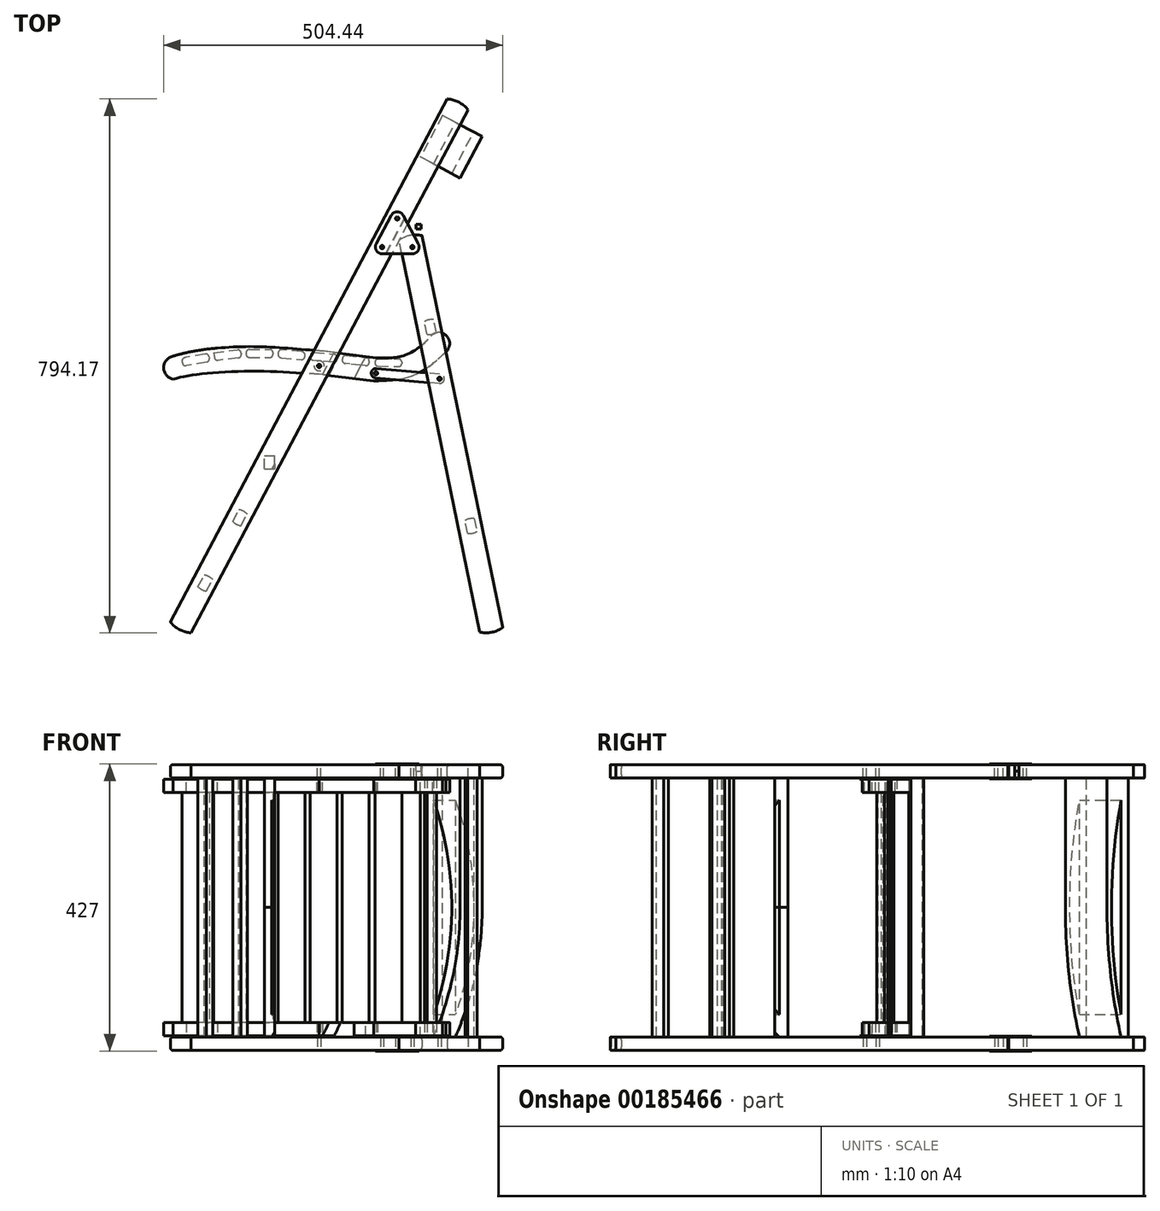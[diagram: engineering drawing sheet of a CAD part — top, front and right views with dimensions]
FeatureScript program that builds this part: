
annotation { "Feature Type Name" : "Feature", "Feature Type Description" : "" }
export const myFeature = defineFeature(function(context is Context, id is Id, definition is map)
    precondition{}
    {
        {
            var Q0;
            Q0=qCreatedBy(makeId("Top.planeOp"),FACE);
            var sketch = newSketch(context, id + "F0", { "sketchPlane" : qUnion([Q0])});
            skCircle(sketch, "E0", {"center": v(0, 0) * mm, "radius": 2.5 * mm});
            skLineSegment(sketch, "E1", {"start": v(-45, 8.94) * mm, "end": v(-45, -5.84) * mm, "construction": true});
            skCircle(sketch, "E2", {"center": v(-45, 0) * mm, "radius": 2.5 * mm});
            skLineSegment(sketch, "E3", {"start": v(-22.5, -17.7) * mm, "end": v(-22.5, 31.56) * mm, "construction": true});
            skLineSegment(sketch, "E4", {"start": v(-31.31, 42.5) * mm, "end": v(-6.98, 42.5) * mm, "construction": true});
            skLineSegment(sketch, "E5", {"start": v(-22.5, 31.56) * mm, "end": v(-22.5, 54.9) * mm, "construction": true});
            skCircle(sketch, "E6", {"center": v(-22.5, 42.5) * mm, "radius": 2.5 * mm});
            skLineSegment(sketch, "E7", {"start": v(-45, 0) * mm, "end": v(-62.32, 10) * mm, "construction": true});
            skLineSegment(sketch, "E8", {"start": v(-22.5, 42.5) * mm, "end": v(-47.11, 56.7) * mm, "construction": true});
            skLineSegment(sketch, "E9", {"start": v(-45, 0) * mm, "end": v(-22.5, 42.5) * mm, "construction": true});
            skPoint(sketch, "E10.start.orphan", {"position": v(-53.66, 5) * mm});
            skLineSegment(sketch, "E11", {"start": v(-33.5, 43.45) * mm, "end": v(-27.36, 54.08) * mm, "construction": true});
            skLineSegment(sketch, "E12", {"start": v(-53.66, 5) * mm, "end": v(-31.16, 47.5) * mm});
            skLineSegment(sketch, "E13.MirrorCS", {"start": v(8.66, 5) * mm, "end": v(-13.84, 47.5) * mm});
            skArc(sketch, "E14", {"start": v(-31.16, 47.5) * mm, "mid": v(-22.5, 52.5) * mm, "end": v(-13.84, 47.5) * mm});
            skLineSegment(sketch, "E15", {"start": v(-45, -10) * mm, "end": v(0, -10) * mm});
            skArc(sketch, "E16", {"start": v(-53.66, 5) * mm, "mid": v(-53.66, -5) * mm, "end": v(-45, -10) * mm});
            skArc(sketch, "E17", {"start": v(0, -10) * mm, "mid": v(8.66, -5) * mm, "end": v(8.66, 5) * mm});
            skLineSegment(sketch, "E18", {"start": v(51.83, 220.3) * mm, "end": v(-83.66, -35.63) * mm});
            skLineSegment(sketch, "E19.MirrorCS", {"start": v(82.76, 203.92) * mm, "end": v(-52.73, -52) * mm});
            skLineSegment(sketch, "E20", {"start": v(-22.5, 42.5) * mm, "end": v(-17.5, 51.16) * mm});
            skLineSegment(sketch, "E21", {"start": v(-22.5, 42.5) * mm, "end": v(72, 221) * mm, "construction": true});
            skArc(sketch, "E22", {"start": v(82.76, 203.92) * mm, "mid": v(69.1, 215.53) * mm, "end": v(51.83, 220.3) * mm});
            skLineSegment(sketch, "E23", {"start": v(51.83, 220.3) * mm, "end": v(-359.91, -557.44) * mm});
            skLineSegment(sketch, "E24", {"start": v(82.76, 203.92) * mm, "end": v(-328.98, -573.81) * mm});
            skLineSegment(sketch, "E25", {"start": v(-230.35, -128.17) * mm, "end": v(-2.2, -248.96) * mm, "construction": true});
            skArc(sketch, "E26.MirrorCS", {"start": v(51.83, 220.3) * mm, "mid": v(69.1, 215.53) * mm, "end": v(82.76, 203.92) * mm});
            skLineSegment(sketch, "E27.MirrorCS", {"start": v(-46.8, -225.34) * mm, "end": v(-274.96, -104.55) * mm, "construction": true});
            skArc(sketch, "E28.MirrorCS", {"start": v(-359.91, -557.44) * mm, "mid": v(-346.26, -569.05) * mm, "end": v(-328.98, -573.81) * mm});
            skArc(sketch, "E29.MirrorCS", {"start": v(-328.98, -573.81) * mm, "mid": v(-346.26, -569.05) * mm, "end": v(-359.91, -557.44) * mm});
            skLineSegment(sketch, "E30", {"start": v(-45, 0) * mm, "end": v(-155.4, -208.52) * mm, "construction": true});
            skCircle(sketch, "E31", {"center": v(-138.58, -176.76) * mm, "radius": 2.5 * mm});
            skArc(sketch, "E32", {"start": v(-112.68, -165.24) * mm, "mid": v(10.1, -199.75) * mm, "end": v(128.76, -153.04) * mm});
            skArc(sketch, "E33", {"start": v(-39.3, -26.62) * mm, "mid": v(29, -111.06) * mm, "end": v(36.3, -219.4) * mm});
            skLineSegment(sketch, "E34", {"start": v(0, 0) * mm, "end": v(40.4, -195.88) * mm, "construction": true});
            skLineSegment(sketch, "E35", {"start": v(40.4, -195.88) * mm, "end": v(43.8, -208.99) * mm, "construction": true});
            skCircle(sketch, "E36", {"center": v(40.4, -195.88) * mm, "radius": 2.5 * mm});
            skSolve(sketch);
        }
        {
            var Q0;
            Q0=makeQuery(id+"F0.imprint","IMPRINT",FACE,{"disambiguationData":[TD([[makeQuery(id+"F0.imprint","IMPRINT",EDGE,{"derivedFrom":sQuery(id+"F0.wireOp",EDGE,"E0")}),-1.0]])]});
            var Q1;
            Q1=makeQuery(id+"F0.imprint","IMPRINT",FACE,{"disambiguationData":[TD([[makeQuery(id+"F0.imprint","IMPRINT",EDGE,{"derivedFrom":sQuery(id+"F0.wireOp",EDGE,"E2")}),-1.0]])]});
            extrude(context, id + "F1", {"entities" : qUnion([Q0, Q1]), "depth" : 1 * mm});
        }
        {
            var Q0;
            {var subQ6=sQuery(id+"F0.wireOp",EDGE,"E12");Q0=makeQuery(id+"F0.imprint","IMPRINT",FACE,{"disambiguationData":[TD([[makeQuery(id+"F0.imprint","IMPRINT",EDGE,{"derivedFrom":subQ6}),1.0]])]});}
            var Q1;
            Q1=makeQuery(id+"F0.imprint","IMPRINT",FACE,{"disambiguationData":[TD([[makeQuery(id+"F0.imprint","IMPRINT",EDGE,{"derivedFrom":sQuery(id+"F0.wireOp",EDGE,"E2")}),-1.0]])]});
            extrude(context, id + "F2", {"entities" : qUnion([Q0, Q1]), "oppositeDirection" : true, "depth" : 20 * mm});
        }
        {
            var Q0;
            Q0=makeQuery(id+"F2.opExtrude","CAP_EDGE",EDGE,{"disambiguationData":[OSD([sQuery(id+"F0.wireOp",EDGE,"E23"),sQuery(id+"F0.wireOp",EDGE,"E18")])],"isStart":true});
            var Q1;
            Q1=makeQuery(id+"F2.opExtrude","CAP_EDGE",EDGE,{"disambiguationData":[OSD([sQuery(id+"F0.wireOp",EDGE,"E23"),sQuery(id+"F0.wireOp",EDGE,"E18")])],"isStart":false});
            fillet(context, id + "F3", {"entities" : qUnion([Q0, Q1]), "radius" : 5 * mm, "tangentPropagation" : true, "allowEdgeOverflow" : false});
        }
        {
            var Q0;
            Q0=qCreatedBy(makeId("Top.planeOp"),FACE);
            var sketch = newSketch(context, id + "F4", { "sketchPlane" : qUnion([Q0])});
            skPoint(sketch, "E37.0", {"position": v(-346.26, -569.05) * mm});
            skArc(sketch, "E38.0", {"start": v(-359.91, -557.44) * mm, "mid": v(-346.26, -569.05) * mm, "end": v(-328.98, -573.81) * mm});
            skLineSegment(sketch, "E39.0", {"start": v(82.76, 203.92) * mm, "end": v(-328.98, -573.81) * mm});
            skLineSegment(sketch, "E40", {"start": v(-409.38, -573.81) * mm, "end": v(185.16, -574.2) * mm, "construction": true});
            skLineSegment(sketch, "E41", {"start": v(185.16, -574.2) * mm, "end": v(553.68, -574.45) * mm, "construction": true});
            skLineSegment(sketch, "E42", {"start": v(0, 0) * mm, "end": v(132.92, -644.4) * mm, "construction": true});
            skLineSegment(sketch, "E43", {"start": v(100.28, -572.76) * mm, "end": v(-19.92, 9.96) * mm});
            skLineSegment(sketch, "E44", {"start": v(-326.85, -532.38) * mm, "end": v(180.53, -532.38) * mm, "construction": true});
            skArc(sketch, "E45", {"start": v(100.28, -572.76) * mm, "mid": v(118.2, -573.01) * mm, "end": v(134.55, -565.69) * mm});
            skArc(sketch, "E46", {"start": v(-19.92, 9.96) * mm, "mid": v(-3.57, 17.3) * mm, "end": v(14.35, 17.03) * mm});
            skLineSegment(sketch, "E47.trimOffspring", {"start": v(14.35, 17.03) * mm, "end": v(134.55, -565.69) * mm});
            skCircle(sketch, "E48", {"center": v(0, 0) * mm, "radius": 2.5 * mm});
            skSolve(sketch);
        }
        {
            var Q0;
            Q0 = qSketchRegion(id + "F4", true);
            extrude(context, id + "F5", {"entities" : qUnion([Q0]), "oppositeDirection" : true, "depth" : 20 * mm});
        }
        {
            var Q0;
            Q0=qCreatedBy(makeId("Top.planeOp"),FACE);
            var sketch = newSketch(context, id + "F6", { "sketchPlane" : qUnion([Q0])});
            skLineSegment(sketch, "E49.bottom", {"start": v(5.4, 33.88) * mm, "end": v(13.3, 33.88) * mm});
            skLineSegment(sketch, "E49.top", {"start": v(5.4, 27.1) * mm, "end": v(13.3, 27.1) * mm});
            skLineSegment(sketch, "E49.left", {"start": v(5.4, 33.88) * mm, "end": v(5.4, 27.1) * mm});
            skLineSegment(sketch, "E49.right", {"start": v(13.3, 33.88) * mm, "end": v(13.3, 27.1) * mm});
            skSolve(sketch);
        }
        {
            var Q0;
            Q0 = qSketchRegion(id + "F6", true);
            extrude(context, id + "F7", {"entities" : qUnion([Q0]), "oppositeDirection" : true, "depth" : 10 * mm});
        }
        {
            var Q0;
            Q0=makeQuery(id+"F7.opExtrude","CAP_FACE",FACE,{"disambiguationData":[OSD([sQuery(id+"F6.wireOp",EDGE,"E49.bottom"),sQuery(id+"F6.wireOp",EDGE,"E49.top"),sQuery(id+"F6.wireOp",EDGE,"E49.left"),sQuery(id+"F6.wireOp",EDGE,"E49.right")])],"isStart":false});
            var sketch = newSketch(context, id + "F8", { "sketchPlane" : qUnion([Q0])});
            skLineSegment(sketch, "E50.bottom", {"start": v(5.4, -33.88) * mm, "end": v(13.3, -33.88) * mm});
            skLineSegment(sketch, "E50.top", {"start": v(5.4, -27.1) * mm, "end": v(13.3, -27.1) * mm});
            skLineSegment(sketch, "E50.left", {"start": v(5.4, -33.88) * mm, "end": v(5.4, -27.1) * mm});
            skLineSegment(sketch, "E50.right", {"start": v(13.3, -33.88) * mm, "end": v(13.3, -27.1) * mm});
            skSolve(sketch);
        }
        {
            var Q0;
            Q0=makeQuery(id+"F1.opExtrude","SWEPT_BODY",BODY,{"disambiguationData":[OSD([sQuery(id+"F0.wireOp",EDGE,"E0"),sQuery(id+"F0.wireOp",EDGE,"E2"),sQuery(id+"F0.wireOp",EDGE,"E6"),sQuery(id+"F0.wireOp",EDGE,"E12"),sQuery(id+"F0.wireOp",EDGE,"E13.MirrorCS"),sQuery(id+"F0.wireOp",EDGE,"E14"),sQuery(id+"F0.wireOp",EDGE,"E15"),sQuery(id+"F0.wireOp",EDGE,"E16"),sQuery(id+"F0.wireOp",EDGE,"E17")])]});
            var Q1;
            Q1=makeQuery(id+"F7.opExtrude","SWEPT_BODY",BODY,{"disambiguationData":[OSD([sQuery(id+"F6.wireOp",EDGE,"E49.bottom"),sQuery(id+"F6.wireOp",EDGE,"E49.top"),sQuery(id+"F6.wireOp",EDGE,"E49.left"),sQuery(id+"F6.wireOp",EDGE,"E49.right")])]});
            var Q2;
            Q2=makeQuery(id+"F8.imprint","IMPRINT",FACE,{"disambiguationData":[TD([[makeQuery(id+"F8.imprint","IMPRINT",EDGE,{"derivedFrom":sQuery(id+"F8.wireOp",EDGE,"E50.bottom")}),1.0]])]});
            mirror(context, id + "F9", {"entities" : qUnion([Q0, Q1]), "mirrorPlane" : qUnion([Q2])});
        }
        {
            var Q0;
            Q0=makeQuery(id+"F0.imprint","IMPRINT",FACE,{"disambiguationData":[TD([[makeQuery(id+"F0.imprint","IMPRINT",EDGE,{"derivedFrom":sQuery(id+"F0.wireOp",EDGE,"E0")}),1.0]])]});
            var Q1;
            {var subQ0=sQuery(id+"F0.wireOp",EDGE,"E36");var subQ1=sQuery(id+"F0.wireOp",EDGE,"E32");var subQ2=makeQuery(id+"F0.imprint","INTERSECT",VERTEX,{"disambiguationData":[OD(0.0)],"derivedFrom":[subQ1,subQ0]});Q1=makeQuery(id+"F0.imprint","IMPRINT",FACE,{"disambiguationData":[TD([[makeQuery(id+"F0.imprint","IMPRINT",EDGE,{"disambiguationData":[TD([[subQ2,1.0]])],"derivedFrom":subQ1}),-1.0]])]});}
            var Q2;
            {var subQ0=sQuery(id+"F0.wireOp",EDGE,"E36");var subQ1=sQuery(id+"F0.wireOp",EDGE,"E32");var subQ2=makeQuery(id+"F0.imprint","INTERSECT",VERTEX,{"disambiguationData":[OD(1.0)],"derivedFrom":[subQ1,subQ0]});Q2=makeQuery(id+"F0.imprint","IMPRINT",FACE,{"disambiguationData":[TD([[makeQuery(id+"F0.imprint","IMPRINT",EDGE,{"disambiguationData":[TD([[subQ2,-1.0]])],"derivedFrom":subQ1}),1.0]])]});}
            var Q3;
            {var subQ0=sQuery(id+"F0.wireOp",EDGE,"E36");var subQ1=sQuery(id+"F0.wireOp",EDGE,"E32");var subQ2=makeQuery(id+"F0.imprint","INTERSECT",VERTEX,{"disambiguationData":[OD(0.0)],"derivedFrom":[subQ1,subQ0]});Q3=makeQuery(id+"F0.imprint","IMPRINT",FACE,{"disambiguationData":[TD([[makeQuery(id+"F0.imprint","IMPRINT",EDGE,{"disambiguationData":[TD([[subQ2,1.0]])],"derivedFrom":subQ1}),1.0]])]});}
            var Q4;
            {var subQ0=sQuery(id+"F0.wireOp",EDGE,"E36");var subQ1=sQuery(id+"F0.wireOp",EDGE,"E32");var subQ2=makeQuery(id+"F0.imprint","INTERSECT",VERTEX,{"disambiguationData":[OD(1.0)],"derivedFrom":[subQ1,subQ0]});Q4=makeQuery(id+"F0.imprint","IMPRINT",FACE,{"disambiguationData":[TD([[makeQuery(id+"F0.imprint","IMPRINT",EDGE,{"disambiguationData":[TD([[subQ2,-1.0]])],"derivedFrom":subQ1}),-1.0]])]});}
            extrude(context, id + "F10", {"entities" : qUnion([Q0, Q1, Q2, Q3, Q4]), "operationType" : NewBodyOperationType.REMOVE, "oppositeDirection" : true, "depth" : 200 * mm});
        }
        {
            var Q0;
            Q0=makeQuery(id+"F5.opExtrude","CAP_EDGE",EDGE,{"disambiguationData":[OSD([sQuery(id+"F4.wireOp",EDGE,"E47.trimOffspring")])],"isStart":true});
            var Q1;
            Q1=makeQuery(id+"F5.opExtrude","CAP_EDGE",EDGE,{"disambiguationData":[OSD([sQuery(id+"F4.wireOp",EDGE,"E47.trimOffspring")])],"isStart":false});
            fillet(context, id + "F11", {"entities" : qUnion([Q0, Q1]), "radius" : 5 * mm, "tangentPropagation" : true, "allowEdgeOverflow" : false});
        }
        {
            var Q0;
            Q0=makeQuery(id+"F2.opExtrude","CAP_FACE",FACE,{"disambiguationData":[OSD([sQuery(id+"F0.wireOp",EDGE,"E2"),sQuery(id+"F0.wireOp",EDGE,"E6"),sQuery(id+"F0.wireOp",EDGE,"E23"),sQuery(id+"F0.wireOp",EDGE,"E24"),sQuery(id+"F0.wireOp",EDGE,"E18"),sQuery(id+"F0.wireOp",EDGE,"E26.MirrorCS"),sQuery(id+"F0.wireOp",EDGE,"E29.MirrorCS"),sQuery(id+"F0.wireOp",EDGE,"E31")])],"isStart":false});
            var sketch = newSketch(context, id + "F12", { "sketchPlane" : qUnion([Q0])});
            skLineSegment(sketch, "E51.0", {"start": v(51.83, -220.3) * mm, "end": v(-359.91, 557.44) * mm});
            skLineSegment(sketch, "E52.0", {"start": v(82.76, -203.92) * mm, "end": v(-328.98, 573.81) * mm});
            skLineSegment(sketch, "E53.0", {"start": v(100.28, 572.76) * mm, "end": v(-19.92, -9.96) * mm});
            skLineSegment(sketch, "E54", {"start": v(-319.26, 506.3) * mm, "end": v(-309.5, 487.86) * mm});
            skLineSegment(sketch, "E55", {"start": v(82.26, 426.01) * mm, "end": v(78.28, 406.7) * mm});
            skLineSegment(sketch, "E56", {"start": v(84.9, 404.17) * mm, "end": v(84.9, 404.17) * mm});
            skLineSegment(sketch, "E57", {"start": v(91.99, 403.88) * mm, "end": v(95.97, 423.18) * mm});
            skPoint(sketch, "E58.0", {"position": v(115.55, 573.47) * mm});
            skLineSegment(sketch, "E59", {"start": v(21.9, 130.1) * mm, "end": v(17.92, 110.8) * mm});
            skLineSegment(sketch, "E60", {"start": v(35.62, 127.27) * mm, "end": v(31.64, 107.97) * mm});
            skArc(sketch, "E61", {"start": v(89.35, 425.72) * mm, "mid": v(85.81, 426.15) * mm, "end": v(82.26, 426.01) * mm});
            skArc(sketch, "E62", {"start": v(89.35, 425.72) * mm, "mid": v(92.76, 424.72) * mm, "end": v(95.97, 423.18) * mm});
            skPoint(sketch, "E63.MirrorCS.start.orphan", {"position": v(89.35, 425.72) * mm});
            skArc(sketch, "E64", {"start": v(91.99, 403.88) * mm, "mid": v(84.9, 404.17) * mm, "end": v(78.28, 406.7) * mm});
            skArc(sketch, "E65", {"start": v(29, 129.8) * mm, "mid": v(25.46, 130.24) * mm, "end": v(21.9, 130.1) * mm});
            skArc(sketch, "E66", {"start": v(21.9, 130.1) * mm, "mid": v(29, 129.8) * mm, "end": v(35.62, 127.27) * mm});
            skArc(sketch, "E67", {"start": v(24.55, 108.26) * mm, "mid": v(28.08, 107.83) * mm, "end": v(31.64, 107.97) * mm});
            skArc(sketch, "E68", {"start": v(31.64, 107.97) * mm, "mid": v(24.55, 108.26) * mm, "end": v(17.92, 110.8) * mm});
            skLineSegment(sketch, "E69", {"start": v(-306.9, 512.85) * mm, "end": v(-297.13, 494.42) * mm});
            skPoint(sketch, "E70.0", {"position": v(-343.85, 570.22) * mm});
            skArc(sketch, "E71", {"start": v(-313.08, 509.57) * mm, "mid": v(-316.08, 507.66) * mm, "end": v(-318.73, 505.29) * mm});
            skArc(sketch, "E72", {"start": v(-318.73, 505.29) * mm, "mid": v(-313.08, 509.57) * mm, "end": v(-306.36, 511.84) * mm});
            skArc(sketch, "E73", {"start": v(-302.78, 490.13) * mm, "mid": v(-299.78, 492.04) * mm, "end": v(-297.13, 494.42) * mm});
            skArc(sketch, "E74", {"start": v(-297.13, 494.42) * mm, "mid": v(-302.78, 490.13) * mm, "end": v(-309.5, 487.86) * mm});
            skArc(sketch, "E75", {"start": v(-251.32, 392.91) * mm, "mid": v(-254.58, 391.5) * mm, "end": v(-258.04, 390.65) * mm});
            skArc(sketch, "E76", {"start": v(-258.04, 390.65) * mm, "mid": v(-251.32, 392.91) * mm, "end": v(-245.66, 397.2) * mm});
            skArc(sketch, "E77", {"start": v(-261.6, 412.36) * mm, "mid": v(-258.34, 413.76) * mm, "end": v(-254.89, 414.62) * mm});
            skArc(sketch, "E78", {"start": v(-254.89, 414.62) * mm, "mid": v(-261.6, 412.36) * mm, "end": v(-267.26, 408.07) * mm});
            skLineSegment(sketch, "E79.trimOffspring", {"start": v(-254.89, 414.62) * mm, "end": v(-245.66, 397.2) * mm});
            skLineSegment(sketch, "E80.trimOffspring", {"start": v(-267.26, 408.07) * mm, "end": v(-258.04, 390.65) * mm});
            skSolve(sketch);
        }
        {
            var Q0;
            Q0 = qSketchRegion(id + "F12", true);
            extrude(context, id + "F13", {"entities" : qUnion([Q0]), "depth" : 385 * mm});
        }
        {
            var Q0;
            Q0=makeQuery(id+"F2.opExtrude","CAP_FACE",FACE,{"disambiguationData":[OSD([sQuery(id+"F0.wireOp",EDGE,"E2"),sQuery(id+"F0.wireOp",EDGE,"E6"),sQuery(id+"F0.wireOp",EDGE,"E23"),sQuery(id+"F0.wireOp",EDGE,"E24"),sQuery(id+"F0.wireOp",EDGE,"E18"),sQuery(id+"F0.wireOp",EDGE,"E26.MirrorCS"),sQuery(id+"F0.wireOp",EDGE,"E29.MirrorCS"),sQuery(id+"F0.wireOp",EDGE,"E31")])],"isStart":false});
            var sketch = newSketch(context, id + "F14", { "sketchPlane" : qUnion([Q0])});
            skLineSegment(sketch, "E81.bottom", {"start": v(-219.73, 329.93) * mm, "end": v(-205.06, 329.93) * mm});
            skLineSegment(sketch, "E81.top", {"start": v(-219.73, 309.99) * mm, "end": v(-205.06, 309.99) * mm});
            skLineSegment(sketch, "E81.left", {"start": v(-219.73, 329.93) * mm, "end": v(-219.73, 309.99) * mm});
            skLineSegment(sketch, "E81.right", {"start": v(-205.06, 329.93) * mm, "end": v(-205.06, 309.99) * mm});
            skSolve(sketch);
        }
        {
            var Q0;
            Q0 = qSketchRegion(id + "F14", true);
            extrude(context, id + "F15", {"entities" : qUnion([Q0]), "depth" : 192.5 * mm});
        }
        {
            var Q0;
            Q0=makeQuery(id+"F15.opExtrude","CAP_FACE",FACE,{"disambiguationData":[OSD([sQuery(id+"F14.wireOp",EDGE,"E81.bottom"),sQuery(id+"F14.wireOp",EDGE,"E81.top"),sQuery(id+"F14.wireOp",EDGE,"E81.left"),sQuery(id+"F14.wireOp",EDGE,"E81.right")])],"isStart":false});
            var sketch = newSketch(context, id + "F16", { "sketchPlane" : qUnion([Q0])});
            skSolve(sketch);
        }
        {
            var Q0;
            Q0=makeQuery(id+"F2.opExtrude","SWEPT_BODY",BODY,{"disambiguationData":[OSD([sQuery(id+"F0.wireOp",EDGE,"E2"),sQuery(id+"F0.wireOp",EDGE,"E6"),sQuery(id+"F0.wireOp",EDGE,"E23"),sQuery(id+"F0.wireOp",EDGE,"E24"),sQuery(id+"F0.wireOp",EDGE,"E18"),sQuery(id+"F0.wireOp",EDGE,"E26.MirrorCS"),sQuery(id+"F0.wireOp",EDGE,"E29.MirrorCS"),sQuery(id+"F0.wireOp",EDGE,"E31")])]});
            var Q1;
            Q1=makeQuery(id+"F5.opExtrude","SWEPT_BODY",BODY,{"disambiguationData":[OSD([sQuery(id+"F4.wireOp",EDGE,"E43"),sQuery(id+"F4.wireOp",EDGE,"E45"),sQuery(id+"F4.wireOp",EDGE,"E46"),sQuery(id+"F4.wireOp",EDGE,"E47.trimOffspring"),sQuery(id+"F4.wireOp",EDGE,"E48")])]});
            var Q2;
            Q2=makeQuery(id+"F9.opPattern","COPY",BODY,{"derivedFrom":makeQuery(id+"F1.opExtrude","SWEPT_BODY",BODY,{"disambiguationData":[OSD([sQuery(id+"F0.wireOp",EDGE,"E0"),sQuery(id+"F0.wireOp",EDGE,"E2"),sQuery(id+"F0.wireOp",EDGE,"E6"),sQuery(id+"F0.wireOp",EDGE,"E12"),sQuery(id+"F0.wireOp",EDGE,"E13.MirrorCS"),sQuery(id+"F0.wireOp",EDGE,"E14"),sQuery(id+"F0.wireOp",EDGE,"E15"),sQuery(id+"F0.wireOp",EDGE,"E16"),sQuery(id+"F0.wireOp",EDGE,"E17")])]}),"instanceName":"1"});
            var Q3;
            Q3=makeQuery(id+"F1.opExtrude","SWEPT_BODY",BODY,{"disambiguationData":[OSD([sQuery(id+"F0.wireOp",EDGE,"E0"),sQuery(id+"F0.wireOp",EDGE,"E2"),sQuery(id+"F0.wireOp",EDGE,"E6"),sQuery(id+"F0.wireOp",EDGE,"E12"),sQuery(id+"F0.wireOp",EDGE,"E13.MirrorCS"),sQuery(id+"F0.wireOp",EDGE,"E14"),sQuery(id+"F0.wireOp",EDGE,"E15"),sQuery(id+"F0.wireOp",EDGE,"E16"),sQuery(id+"F0.wireOp",EDGE,"E17")])]});
            var Q4;
            Q4=makeQuery(id+"F13.opExtrude","SWEPT_BODY",BODY,{"disambiguationData":[OSD([sQuery(id+"F12.wireOp",EDGE,"E55"),sQuery(id+"F12.wireOp",EDGE,"E57"),sQuery(id+"F12.wireOp",EDGE,"E61"),sQuery(id+"F12.wireOp",EDGE,"E62"),sQuery(id+"F12.wireOp",EDGE,"E64")])]});
            var Q5;
            Q5=makeQuery(id+"F13.opExtrude","SWEPT_BODY",BODY,{"disambiguationData":[OSD([sQuery(id+"F12.wireOp",EDGE,"E59"),sQuery(id+"F12.wireOp",EDGE,"E60"),sQuery(id+"F12.wireOp",EDGE,"E66"),sQuery(id+"F12.wireOp",EDGE,"E68")])]});
            var Q6;
            Q6=makeQuery(id+"F13.opExtrude","SWEPT_BODY",BODY,{"disambiguationData":[OSD([sQuery(id+"F12.wireOp",EDGE,"E54"),sQuery(id+"F12.wireOp",EDGE,"E69"),sQuery(id+"F12.wireOp",EDGE,"E72"),sQuery(id+"F12.wireOp",EDGE,"E74")])]});
            var Q7;
            Q7=makeQuery(id+"F15.opExtrude","SWEPT_BODY",BODY,{"disambiguationData":[OSD([sQuery(id+"F14.wireOp",EDGE,"E81.bottom"),sQuery(id+"F14.wireOp",EDGE,"E81.top"),sQuery(id+"F14.wireOp",EDGE,"E81.left"),sQuery(id+"F14.wireOp",EDGE,"E81.right")])]});
            var Q8;
            Q8=makeQuery(id+"F13.opExtrude","SWEPT_BODY",BODY,{"disambiguationData":[OSD([sQuery(id+"F12.wireOp",EDGE,"E76"),sQuery(id+"F12.wireOp",EDGE,"E78"),sQuery(id+"F12.wireOp",EDGE,"E79.trimOffspring"),sQuery(id+"F12.wireOp",EDGE,"E80.trimOffspring")])]});
            var Q9;
            Q9=makeQuery(id+"F16.imprint","IMPRINT",FACE,{"disambiguationData":[TD([[makeQuery(id+"F16.imprint","IMPRINT",EDGE,{"derivedFrom":makeQuery(id+"F15.opExtrude","CAP_EDGE",EDGE,{"disambiguationData":[OSD([sQuery(id+"F14.wireOp",EDGE,"E81.bottom")])],"isStart":false})}),-1.0]])]});
            mirror(context, id + "F17", {"entities" : qUnion([Q0, Q1, Q2, Q3, Q4, Q5, Q6, Q7, Q8]), "mirrorPlane" : qUnion([Q9])});
        }
        {
            var Q0;
            Q0=makeQuery(id+"F5.opExtrude","CAP_FACE",FACE,{"disambiguationData":[OSD([sQuery(id+"F4.wireOp",EDGE,"E43"),sQuery(id+"F4.wireOp",EDGE,"E45"),sQuery(id+"F4.wireOp",EDGE,"E46"),sQuery(id+"F4.wireOp",EDGE,"E47.trimOffspring"),sQuery(id+"F4.wireOp",EDGE,"E48")])],"isStart":false});
            var sketch = newSketch(context, id + "F18", { "sketchPlane" : qUnion([Q0])});
            skCircle(sketch, "E82.0", {"center": v(40.4, 195.88) * mm, "radius": 2.5 * mm});
            skArc(sketch, "E83", {"start": v(-49.74, 165.88) * mm, "mid": v(-52.25, 216.86) * mm, "end": v(-28.02, 261.78) * mm, "construction": true});
            skLineSegment(sketch, "E84", {"start": v(118.73, 195.88) * mm, "end": v(-61.62, 195.88) * mm, "construction": true});
            skLineSegment(sketch, "E85", {"start": v(40.4, 195.88) * mm, "end": v(-61.21, 186.99) * mm, "construction": true});
            skCircle(sketch, "E86", {"center": v(-54.23, 187.6) * mm, "radius": 2.5 * mm});
            skLineSegment(sketch, "E87", {"start": v(41.62, 188.96) * mm, "end": v(-53.88, 180.6) * mm});
            skLineSegment(sketch, "E88.MirrorCS", {"start": v(40.4, 202.9) * mm, "end": v(-55.1, 194.55) * mm});
            skArc(sketch, "E89", {"start": v(-53.37, 180.65) * mm, "mid": v(-61.21, 186.99) * mm, "end": v(-54.59, 194.6) * mm});
            skArc(sketch, "E90", {"start": v(40.4, 188.85) * mm, "mid": v(47.43, 195.88) * mm, "end": v(40.4, 202.9) * mm});
            skSolve(sketch);
        }
        {
            var Q0;
            Q0 = qSketchRegion(id + "F18", true);
            extrude(context, id + "F19", {"entities" : qUnion([Q0]), "depth" : 1.5 * mm});
        }
        {
            var Q0;
            Q0=makeQuery(id+"F19.opExtrude","SWEPT_BODY",BODY,{"disambiguationData":[OSD([sQuery(id+"F18.wireOp",EDGE,"E86"),sQuery(id+"F18.wireOp",EDGE,"E87"),sQuery(id+"F18.wireOp",EDGE,"E88.MirrorCS"),sQuery(id+"F18.wireOp",EDGE,"E89"),sQuery(id+"F18.wireOp",EDGE,"E90"),sQuery(id+"F18.wireOp",EDGE,"E82.0")])]});
            var Q1;
            Q1=makeQuery(id+"F17.opPattern","COPY",FACE,{"derivedFrom":makeQuery(id+"F15.opExtrude","CAP_FACE",FACE,{"disambiguationData":[OSD([sQuery(id+"F14.wireOp",EDGE,"E81.bottom"),sQuery(id+"F14.wireOp",EDGE,"E81.top"),sQuery(id+"F14.wireOp",EDGE,"E81.left"),sQuery(id+"F14.wireOp",EDGE,"E81.right")])],"isStart":false}),"instanceName":"1"});
            mirror(context, id + "F20", {"entities" : qUnion([Q0]), "mirrorPlane" : qUnion([Q1])});
        }
        {
            var Q0;
            Q0=makeQuery(id+"F2.opExtrude","CAP_FACE",FACE,{"disambiguationData":[OSD([sQuery(id+"F0.wireOp",EDGE,"E2"),sQuery(id+"F0.wireOp",EDGE,"E6"),sQuery(id+"F0.wireOp",EDGE,"E23"),sQuery(id+"F0.wireOp",EDGE,"E24"),sQuery(id+"F0.wireOp",EDGE,"E18"),sQuery(id+"F0.wireOp",EDGE,"E26.MirrorCS"),sQuery(id+"F0.wireOp",EDGE,"E29.MirrorCS"),sQuery(id+"F0.wireOp",EDGE,"E31")])],"isStart":false});
            var sketch = newSketch(context, id + "F21", { "sketchPlane" : qUnion([Q0])});
            skCircle(sketch, "E91", {"center": v(-138.58, 176.76) * mm, "radius": 2.5 * mm});
            skCircle(sketch, "E92", {"center": v(-138.58, 176.76) * mm, "radius": 7.5 * mm});
            skSolve(sketch);
        }
        {
            var Q0;
            Q0 = qSketchRegion(id + "F21", true);
            extrude(context, id + "F22", {"entities" : qUnion([Q0]), "depth" : 1.5 * mm});
        }
        {
            var Q0;
            Q0=makeQuery(id+"F19.opExtrude","CAP_FACE",FACE,{"disambiguationData":[OSD([sQuery(id+"F18.wireOp",EDGE,"E86"),sQuery(id+"F18.wireOp",EDGE,"E87"),sQuery(id+"F18.wireOp",EDGE,"E88.MirrorCS"),sQuery(id+"F18.wireOp",EDGE,"E89"),sQuery(id+"F18.wireOp",EDGE,"E90"),sQuery(id+"F18.wireOp",EDGE,"E82.0")])],"isStart":false});
            var sketch = newSketch(context, id + "F23", { "sketchPlane" : qUnion([Q0])});
            skArc(sketch, "E93", {"start": v(64.27, 168.7) * mm, "mid": v(29.96, 102.09) * mm, "end": v(-37.18, 68.81) * mm, "construction": true});
            skLineSegment(sketch, "E94", {"start": v(-57.48, 199.15) * mm, "end": v(-57.54, 199.14) * mm});
            skPoint(sketch, "E94.endSnap0", {"position": v(-138.54, 189.15) * mm});
            skPoint(sketch, "E95.endSnap0", {"position": v(-133.82, 154.74) * mm});
            skPoint(sketch, "E96.trimOffspring.end.orphan", {"position": v(-145.21, 154.74) * mm});
            skLineSegment(sketch, "E97", {"start": v(-53.82, 164.6) * mm, "end": v(-133.82, 154.74) * mm});
            skLineSegment(sketch, "E98", {"start": v(-57.48, 199.15) * mm, "end": v(-138.54, 189.15) * mm});
            skArc(sketch, "E99", {"start": v(47.11, 172.28) * mm, "mid": v(25.17, 122.78) * mm, "end": v(-18.93, 91.37) * mm, "construction": true});
            skFitSpline(sketch, "E100", {"points": [v(-53.82, 164.6) * mm, v(0, 155.78) * mm, v(30.24, 129.54) * mm, v(30.22, 129.52) * mm], "startDerivative": vector(101.7, 4.07) * mm, "endDerivative": vector(-2.24, -0.94) * mm});
            skArc(sketch, "E101", {"start": v(30.24, 129.54) * mm, "mid": v(52.29, 133.76) * mm, "end": v(49.6, 156.05) * mm});
            skFitSpline(sketch, "E102", {"points": [v(-57.54, 199.14) * mm, v(4.84, 189.2) * mm, v(49.6, 156.05) * mm], "startDerivative": vector(128.56, -6.46) * mm, "endDerivative": vector(85.52, -80.44) * mm});
            skFitSpline(sketch, "E103", {"points": [v(-133.82, 154.74) * mm, v(-243.2, 148.03) * mm, v(-324.06, 154.74) * mm, v(-356.53, 162.44) * mm], "startDerivative": vector(-266.22, -22.84) * mm, "endDerivative": vector(-122.92, 37.02) * mm});
            skLineSegment(sketch, "E104", {"start": v(-138.54, 189.15) * mm, "end": v(-138.54, 189.15) * mm});
            skFitSpline(sketch, "E105", {"points": [v(-138.54, 189.15) * mm, v(-231.03, 184.64) * mm, v(-317.3, 189.15) * mm, v(-356.14, 196.54) * mm], "startDerivative": vector(-237.1, -15.36) * mm, "endDerivative": vector(-134.36, 39.6) * mm});
            skArc(sketch, "E106", {"start": v(-356.14, 196.54) * mm, "mid": v(-369.9, 179.56) * mm, "end": v(-356.36, 162.4) * mm});
            skFitSpline(sketch, "E107", {"points": [v(-133.82, 154.74) * mm, v(-221.72, 148.83) * mm, v(-296.47, 150.88) * mm, v(-338.72, 157.7) * mm, v(-356.36, 162.4) * mm, v(-356.42, 162.42) * mm], "startDerivative": vector(-276.14, -22.14) * mm, "endDerivative": vector(-3.9, 0.81) * mm});
            skCircle(sketch, "E108", {"center": v(-54.23, 187.6) * mm, "radius": 2.5 * mm});
            skCircle(sketch, "E109", {"center": v(-139.52, 177.02) * mm, "radius": 2.5 * mm});
            skPoint(sketch, "E110.orphan", {"position": v(-66.23, 187.6) * mm});
            skLineSegment(sketch, "E111.trimOffspring", {"start": v(-57.54, 199.14) * mm, "end": v(-57.54, 199.14) * mm});
            skPoint(sketch, "E112.orphan", {"position": v(-151.52, 177.02) * mm});
            skFitSpline(sketch, "E113", {"points": [v(-57.48, 199.15) * mm, v(-35.44, 198.03) * mm, v(4.84, 189.2) * mm, v(44.67, 160.68) * mm, v(49.6, 156.05) * mm], "startDerivative": vector(90.74, -3.96) * mm, "endDerivative": vector(28.38, -27.6) * mm});
            skSolve(sketch);
        }
        {
            var Q0;
            Q0 = qSketchRegion(id + "F23", true);
            extrude(context, id + "F24", {"entities" : qUnion([Q0]), "depth" : 20 * mm});
        }
        {
            var Q0;
            Q0=makeQuery(id+"F24.opExtrude","SWEPT_BODY",BODY,{"disambiguationData":[OSD([sQuery(id+"F23.wireOp",EDGE,"E97"),sQuery(id+"F23.wireOp",EDGE,"E98"),sQuery(id+"F23.wireOp",EDGE,"E100"),sQuery(id+"F23.wireOp",EDGE,"E101"),sQuery(id+"F23.wireOp",EDGE,"E105"),sQuery(id+"F23.wireOp",EDGE,"E106"),sQuery(id+"F23.wireOp",EDGE,"E107"),sQuery(id+"F23.wireOp",EDGE,"E108"),sQuery(id+"F23.wireOp",EDGE,"E109"),sQuery(id+"F23.wireOp",EDGE,"E113")])]});
            var Q1;
            Q1=makeQuery(id+"F17.opPattern","COPY",FACE,{"derivedFrom":makeQuery(id+"F15.opExtrude","CAP_FACE",FACE,{"disambiguationData":[OSD([sQuery(id+"F14.wireOp",EDGE,"E81.bottom"),sQuery(id+"F14.wireOp",EDGE,"E81.top"),sQuery(id+"F14.wireOp",EDGE,"E81.left"),sQuery(id+"F14.wireOp",EDGE,"E81.right")])],"isStart":false}),"instanceName":"1"});
            mirror(context, id + "F25", {"entities" : qUnion([Q0]), "mirrorPlane" : qUnion([Q1])});
        }
        {
            var Q0;
            Q0=makeQuery(id+"F17.opPattern","COPY",FACE,{"derivedFrom":makeQuery(id+"F2.opExtrude","SWEPT_FACE",FACE,{"disambiguationData":[OSD([sQuery(id+"F0.wireOp",EDGE,"E24")])]}),"instanceName":"1"});
            var sketch = newSketch(context, id + "F26", { "sketchPlane" : qUnion([Q0])});
            skLineSegment(sketch, "E114.0", {"start": v(218.95, -405) * mm, "end": v(-661.05, -405) * mm});
            skLineSegment(sketch, "E115.0", {"start": v(218.95, -20) * mm, "end": v(-661.05, -20) * mm});
            skPoint(sketch, "E116.0", {"position": v(218.95, -415) * mm});
            skPoint(sketch, "E117.0", {"position": v(218.95, 0) * mm});
            skLineSegment(sketch, "E118.0", {"start": v(218.95, -20) * mm, "end": v(218.95, 0) * mm});
            skLineSegment(sketch, "E119.bottom", {"start": v(193.95, -405) * mm, "end": v(123.95, -405) * mm});
            skLineSegment(sketch, "E119.top", {"start": v(193.95, -20) * mm, "end": v(123.95, -20) * mm});
            skLineSegment(sketch, "E119.left", {"start": v(193.95, -405) * mm, "end": v(193.95, -20) * mm});
            skLineSegment(sketch, "E119.right", {"start": v(123.95, -405) * mm, "end": v(123.95, -20) * mm});
            skSolve(sketch);
        }
        {
            var Q0;
            Q0 = qSketchRegion(id + "F26", true);
            extrude(context, id + "F27", {"entities" : qUnion([Q0]), "depth" : 37 * mm});
        }
        {
            var Q0;
            Q0=makeQuery(id+"F27.opExtrude","CAP_FACE",FACE,{"disambiguationData":[OSD([sQuery(id+"F26.wireOp",EDGE,"E119.bottom"),sQuery(id+"F26.wireOp",EDGE,"E119.top"),sQuery(id+"F26.wireOp",EDGE,"E119.left"),sQuery(id+"F26.wireOp",EDGE,"E119.right")])],"isStart":true});
            extrude(context, id + "F28", {"entities" : qUnion([Q0]), "operationType" : NewBodyOperationType.ADD, "depth" : 30 * mm});
        }
        {
            var Q0;
            {var subQ0=sQuery(id+"F26.wireOp",EDGE,"E119.left");Q0=makeQuery(id+"F28.boolean.opBoolean","MERGE",FACE,{"derivedFrom":[makeQuery(id+"F27.opExtrude","SWEPT_FACE",FACE,{"disambiguationData":[OSD([subQ0])]}),makeQuery(id+"F28.opExtrude","SWEPT_FACE",FACE,{"disambiguationData":[OSD([subQ0])]})]});}
            var sketch = newSketch(context, id + "F29", { "sketchPlane" : qUnion([Q0])});
            skLineSegment(sketch, "E120.0", {"start": v(-14.73, -405) * mm, "end": v(-14.73, -20) * mm});
            skLineSegment(sketch, "E121.0", {"start": v(52.27, -405) * mm, "end": v(52.27, -20) * mm});
            skPoint(sketch, "E122.0", {"position": v(3.77, -20) * mm});
            skLineSegment(sketch, "E123.0", {"start": v(-14.73, -20) * mm, "end": v(22.27, -20) * mm});
            skLineSegment(sketch, "E124.0", {"start": v(-14.73, -405) * mm, "end": v(22.27, -405) * mm});
            skLineSegment(sketch, "E125.0", {"start": v(22.27, -405) * mm, "end": v(52.27, -405) * mm});
            skLineSegment(sketch, "E126.0", {"start": v(22.27, -20) * mm, "end": v(52.27, -20) * mm});
            skLineSegment(sketch, "E127.bottom", {"start": v(52.27, -20) * mm, "end": v(45.27, -20) * mm});
            skLineSegment(sketch, "E127.top", {"start": v(52.27, -405) * mm, "end": v(45.27, -405) * mm});
            skLineSegment(sketch, "E127.left", {"start": v(52.27, -20) * mm, "end": v(52.27, -405) * mm});
            skLineSegment(sketch, "E127.right", {"start": v(45.27, -20) * mm, "end": v(45.27, -405) * mm});
            skLineSegment(sketch, "E128.bottom", {"start": v(45.27, -20) * mm, "end": v(30.27, -20) * mm});
            skLineSegment(sketch, "E128.top", {"start": v(45.27, -405) * mm, "end": v(30.27, -405) * mm});
            skLineSegment(sketch, "E128.right", {"start": v(30.27, -20) * mm, "end": v(30.27, -405) * mm});
            skLineSegment(sketch, "E129", {"start": v(-26.33, -212.5) * mm, "end": v(22.1, -212.5) * mm, "construction": true});
            skPoint(sketch, "E129.startSnap0", {"position": v(-14.73, -212.5) * mm});
            skLineSegment(sketch, "E130.0.3", {"start": v(52.27, -20) * mm, "end": v(22.27, -20) * mm});
            skLineSegment(sketch, "E130.0.4", {"start": v(22.27, -20) * mm, "end": v(-14.73, -20) * mm});
            skLineSegment(sketch, "E130.0.5", {"start": v(-14.73, -20) * mm, "end": v(-14.73, -405) * mm});
            skLineSegment(sketch, "E131", {"start": v(0.27, -253.46) * mm, "end": v(0.27, -170.3) * mm, "construction": true});
            skArc(sketch, "E132", {"start": v(30.27, -20) * mm, "mid": v(-14.73, -212.5) * mm, "end": v(30.27, -405) * mm});
            skArc(sketch, "E133", {"start": v(45.27, -20) * mm, "mid": v(-0.57, -212.5) * mm, "end": v(45.27, -405) * mm});
            skSolve(sketch);
        }
        {
            var Q0;
            {var subQ0=sQuery(id+"F29.wireOp",EDGE,"E124.0");Q0=makeQuery(id+"F29.imprint","IMPRINT",FACE,{"disambiguationData":[TD([[makeQuery(id+"F29.imprint","IMPRINT",EDGE,{"derivedFrom":subQ0}),1.0]])]});}
            var Q1;
            {var subQ0=sQuery(id+"F29.wireOp",EDGE,"E130.0.4");Q1=makeQuery(id+"F29.imprint","IMPRINT",FACE,{"disambiguationData":[TD([[makeQuery(id+"F29.imprint","IMPRINT",EDGE,{"derivedFrom":subQ0}),-1.0]])]});}
            var Q2;
            {var subQ0=sQuery(id+"F29.wireOp",EDGE,"E133");var subQ1=sQuery(id+"F29.wireOp",EDGE,"E128.right");var subQ2=makeQuery(id+"F29.imprint","INTERSECT",VERTEX,{"disambiguationData":[OD(0.0)],"derivedFrom":[subQ1,subQ0]});Q2=makeQuery(id+"F29.imprint","IMPRINT",FACE,{"disambiguationData":[TD([[makeQuery(id+"F29.imprint","IMPRINT",EDGE,{"disambiguationData":[TD([[subQ2,-1.0]])],"derivedFrom":subQ1}),-1.0]])]});}
            var Q3;
            {var subQ0=sQuery(id+"F29.wireOp",EDGE,"E127.right");Q3=makeQuery(id+"F29.imprint","IMPRINT",FACE,{"disambiguationData":[TD([[makeQuery(id+"F29.imprint","IMPRINT",EDGE,{"derivedFrom":subQ0}),-1.0]])]});}
            var Q4;
            {var subQ0=sQuery(id+"F29.wireOp",EDGE,"E127.right");Q4=makeQuery(id+"F29.imprint","IMPRINT",FACE,{"disambiguationData":[TD([[makeQuery(id+"F29.imprint","IMPRINT",EDGE,{"derivedFrom":subQ0}),1.0]])]});}
            extrude(context, id + "F30", {"entities" : qUnion([Q0, Q1, Q2, Q3, Q4]), "operationType" : NewBodyOperationType.REMOVE, "oppositeDirection" : true, "depth" : 800 * mm});
        }
        {
            var Q0;
            Q0=makeQuery(id+"F25.opPattern","COPY",FACE,{"derivedFrom":makeQuery(id+"F24.opExtrude","CAP_FACE",FACE,{"disambiguationData":[OSD([sQuery(id+"F23.wireOp",EDGE,"E97"),sQuery(id+"F23.wireOp",EDGE,"E98"),sQuery(id+"F23.wireOp",EDGE,"E100"),sQuery(id+"F23.wireOp",EDGE,"E101"),sQuery(id+"F23.wireOp",EDGE,"E105"),sQuery(id+"F23.wireOp",EDGE,"E106"),sQuery(id+"F23.wireOp",EDGE,"E107"),sQuery(id+"F23.wireOp",EDGE,"E108"),sQuery(id+"F23.wireOp",EDGE,"E109"),sQuery(id+"F23.wireOp",EDGE,"E113")])],"isStart":false}),"instanceName":"1"});
            var sketch = newSketch(context, id + "F31", { "sketchPlane" : qUnion([Q0])});
            skFitSpline(sketch, "E134", {"points": [v(-347.6, -174.12) * mm, v(-318.74, -165.66) * mm, v(-268.5, -161.15) * mm, v(-208.15, -160.19) * mm, v(-131.16, -165.59) * mm, v(-53.24, -174.32) * mm, v(-16.91, -174.16) * mm, v(12.67, -163.38) * mm, v(31.32, -147.41) * mm], "startDerivative": vector(265.71, 94.58) * mm, "endDerivative": vector(185.33, 187.9) * mm, "construction": true});
            skArc(sketch, "E135.0", {"start": v(-356.14, -196.54) * mm, "mid": v(-369.9, -179.56) * mm, "end": v(-356.36, -162.4) * mm, "construction": true});
            skPoint(sketch, "E136.0", {"position": v(-369.9, -179.56) * mm});
            skLineSegment(sketch, "E137", {"start": v(-353.54, -141.67) * mm, "end": v(-329.3, -198) * mm, "construction": true});
            skLineSegment(sketch, "E138", {"start": v(-305.52, -151.87) * mm, "end": v(-313.33, -129.55) * mm, "construction": true});
            skPoint(sketch, "E139.startSnap0", {"position": v(-309.42, -140.71) * mm});
            skLineSegment(sketch, "E140", {"start": v(-303.31, -158.17) * mm, "end": v(-343.31, -165.44) * mm});
            skLineSegment(sketch, "E141", {"start": v(-301.13, -170.17) * mm, "end": v(-341.13, -177.44) * mm});
            skLineSegment(sketch, "E142", {"start": v(-303.31, -158.17) * mm, "end": v(-301.13, -170.17) * mm});
            skLineSegment(sketch, "E143", {"start": v(-343.31, -165.44) * mm, "end": v(-341.13, -177.44) * mm});
            skLineSegment(sketch, "E144", {"start": v(-295.31, -157.08) * mm, "end": v(-293.9, -169) * mm});
            skLineSegment(sketch, "E145", {"start": v(-295.31, -157.08) * mm, "end": v(-255.31, -152.31) * mm});
            skLineSegment(sketch, "E146", {"start": v(-255.31, -152.31) * mm, "end": v(-253.9, -164.23) * mm});
            skLineSegment(sketch, "E147", {"start": v(-253.9, -164.23) * mm, "end": v(-293.9, -169) * mm});
            skLineSegment(sketch, "E148.bottom", {"start": v(-247.25, -152.31) * mm, "end": v(-207.25, -152.31) * mm});
            skLineSegment(sketch, "E148.top", {"start": v(-247.25, -164.31) * mm, "end": v(-207.25, -164.31) * mm});
            skLineSegment(sketch, "E148.left", {"start": v(-247.25, -152.31) * mm, "end": v(-247.25, -164.31) * mm});
            skLineSegment(sketch, "E148.right", {"start": v(-207.25, -152.31) * mm, "end": v(-207.25, -164.31) * mm});
            skLineSegment(sketch, "E149", {"start": v(-200.16, -164.11) * mm, "end": v(-160.34, -167.9) * mm});
            skLineSegment(sketch, "E150", {"start": v(-160.34, -167.9) * mm, "end": v(-159.22, -156.1) * mm});
            skLineSegment(sketch, "E151", {"start": v(-159.22, -156.1) * mm, "end": v(-199.04, -152.31) * mm});
            skLineSegment(sketch, "E152", {"start": v(-199.04, -152.31) * mm, "end": v(-200.16, -164.11) * mm});
            skLineSegment(sketch, "E153", {"start": v(-151.18, -156.1) * mm, "end": v(-152.32, -168.05) * mm});
            skLineSegment(sketch, "E154", {"start": v(-151.18, -156.1) * mm, "end": v(-111.36, -159.9) * mm});
            skLineSegment(sketch, "E155", {"start": v(-111.36, -159.9) * mm, "end": v(-112.5, -171.84) * mm});
            skLineSegment(sketch, "E156", {"start": v(-112.5, -171.84) * mm, "end": v(-152.32, -168.05) * mm});
            skPoint(sketch, "E157.orphan", {"position": v(-152.3, -167.9) * mm});
            skLineSegment(sketch, "E158", {"start": v(-103.4, -160.76) * mm, "end": v(-63.64, -165.1) * mm});
            skLineSegment(sketch, "E159", {"start": v(-63.64, -165.1) * mm, "end": v(-64.95, -177.04) * mm});
            skLineSegment(sketch, "E160", {"start": v(-103.4, -160.76) * mm, "end": v(-104.75, -173.08) * mm});
            skLineSegment(sketch, "E161", {"start": v(-64.95, -177.04) * mm, "end": v(-104.71, -172.69) * mm});
            skLineSegment(sketch, "E162", {"start": v(-55.74, -166.45) * mm, "end": v(-55.74, -177.1) * mm});
            skLineSegment(sketch, "E163", {"start": v(-55.74, -166.45) * mm, "end": v(-15.74, -166.45) * mm});
            skLineSegment(sketch, "E164", {"start": v(-15.74, -166.45) * mm, "end": v(-15.74, -177.95) * mm});
            skLineSegment(sketch, "E165", {"start": v(-55.74, -177.1) * mm, "end": v(-15.74, -177.95) * mm});
            skSolve(sketch);
        }
        {
            var Q0;
            Q0 = qSketchRegion(id + "F31", true);
            extrude(context, id + "F32", {"entities" : qUnion([Q0]), "operationType" : NewBodyOperationType.ADD, "depth" : 345 * mm});
        }
        {
            var Q0;
            Q0=makeQuery(id+"F32.opExtrude","SWEPT_EDGE",EDGE,{"disambiguationData":[OSD([sQuery(id+"F31.wireOp",EDGE,"E163"),sQuery(id+"F31.wireOp",EDGE,"E164")])]});
            var Q1;
            Q1=makeQuery(id+"F32.opExtrude","SWEPT_EDGE",EDGE,{"disambiguationData":[OSD([sQuery(id+"F31.wireOp",EDGE,"E162"),sQuery(id+"F31.wireOp",EDGE,"E163")])]});
            var Q2;
            Q2=makeQuery(id+"F32.opExtrude","SWEPT_EDGE",EDGE,{"disambiguationData":[OSD([sQuery(id+"F31.wireOp",EDGE,"E158"),sQuery(id+"F31.wireOp",EDGE,"E159")])]});
            var Q3;
            Q3=makeQuery(id+"F32.opExtrude","SWEPT_EDGE",EDGE,{"disambiguationData":[OSD([sQuery(id+"F31.wireOp",EDGE,"E158"),sQuery(id+"F31.wireOp",EDGE,"E160")])]});
            var Q4;
            Q4=makeQuery(id+"F32.opExtrude","SWEPT_EDGE",EDGE,{"disambiguationData":[OSD([sQuery(id+"F31.wireOp",EDGE,"E154"),sQuery(id+"F31.wireOp",EDGE,"E155")])]});
            var Q5;
            Q5=makeQuery(id+"F32.opExtrude","SWEPT_EDGE",EDGE,{"disambiguationData":[OSD([sQuery(id+"F31.wireOp",EDGE,"E153"),sQuery(id+"F31.wireOp",EDGE,"E154")])]});
            var Q6;
            Q6=makeQuery(id+"F32.opExtrude","SWEPT_EDGE",EDGE,{"disambiguationData":[OSD([sQuery(id+"F31.wireOp",EDGE,"E150"),sQuery(id+"F31.wireOp",EDGE,"E151")])]});
            var Q7;
            Q7=makeQuery(id+"F32.opExtrude","SWEPT_EDGE",EDGE,{"disambiguationData":[OSD([sQuery(id+"F31.wireOp",EDGE,"E151"),sQuery(id+"F31.wireOp",EDGE,"E152")])]});
            var Q8;
            Q8=makeQuery(id+"F32.opExtrude","SWEPT_EDGE",EDGE,{"disambiguationData":[OSD([sQuery(id+"F31.wireOp",EDGE,"E148.bottom"),sQuery(id+"F31.wireOp",EDGE,"E148.right")])]});
            var Q9;
            Q9=makeQuery(id+"F32.opExtrude","SWEPT_EDGE",EDGE,{"disambiguationData":[OSD([sQuery(id+"F31.wireOp",EDGE,"E148.bottom"),sQuery(id+"F31.wireOp",EDGE,"E148.left")])]});
            var Q10;
            Q10=makeQuery(id+"F32.opExtrude","SWEPT_EDGE",EDGE,{"disambiguationData":[OSD([sQuery(id+"F31.wireOp",EDGE,"E145"),sQuery(id+"F31.wireOp",EDGE,"E146")])]});
            var Q11;
            {var subQ0=sQuery(id+"F26.wireOp",EDGE,"E119.left");var subQ1=makeQuery(id+"F27.opExtrude","SWEPT_FACE",FACE,{"disambiguationData":[OSD([subQ0])]});var subQ2=sQuery(id+"F0.wireOp",EDGE,"E29.MirrorCS");var subQ3=sQuery(id+"F0.wireOp",EDGE,"E26.MirrorCS");var subQ4=sQuery(id+"F0.wireOp",EDGE,"E24");var subQ5=makeQuery(id+"F2.opExtrude","CAP_FACE",FACE,{"disambiguationData":[OSD([sQuery(id+"F0.wireOp",EDGE,"E2"),sQuery(id+"F0.wireOp",EDGE,"E6"),sQuery(id+"F0.wireOp",EDGE,"E23"),subQ4,sQuery(id+"F0.wireOp",EDGE,"E18"),subQ3,subQ2,sQuery(id+"F0.wireOp",EDGE,"E31")])],"isStart":false});var subQ6=makeQuery(id+"F2.opExtrude","SWEPT_FACE",FACE,{"disambiguationData":[OSD([subQ4])]});var subQ7=sQuery(id+"F26.wireOp",EDGE,"E119.top");var subQ8=makeQuery(id+"F27.opExtrude","SWEPT_FACE",FACE,{"disambiguationData":[OSD([subQ7])]});var subQ9=sQuery(id+"F26.wireOp",EDGE,"E119.right");var subQ10=makeQuery(id+"F27.opExtrude","SWEPT_FACE",FACE,{"disambiguationData":[OSD([subQ9])]});var subQ11=makeQuery(id+"F28.opExtrude","SWEPT_FACE",FACE,{"disambiguationData":[OSD([subQ7])]});var subQ12=makeQuery(id+"F28.opExtrude","SWEPT_FACE",FACE,{"disambiguationData":[OSD([subQ0])]});var subQ13=makeQuery(id+"F28.opExtrude","SWEPT_FACE",FACE,{"disambiguationData":[OSD([subQ9])]});var subQ14=makeQuery(id+"F2.opExtrude","CAP_EDGE",EDGE,{"disambiguationData":[OSD([subQ4])],"isStart":false});Q11=makeQuery(id+"F30.boolean.opBoolean","MERGE",EDGE,{"derivedFrom":[makeQuery(id+"F28.boolean.opBoolean","SPLIT",EDGE,{"disambiguationData":[TD([subQ5,subQ6,makeQuery(id+"F2.opExtrude","SWEPT_FACE",FACE,{"disambiguationData":[OSD([subQ3])]}),subQ8,subQ1,subQ11,subQ12])],"derivedFrom":subQ14}),makeQuery(id+"F28.boolean.opBoolean","SPLIT",EDGE,{"disambiguationData":[TD([subQ5,subQ6,makeQuery(id+"F2.opExtrude","SWEPT_FACE",FACE,{"disambiguationData":[OSD([subQ2])]}),subQ8,subQ10,subQ11,subQ13])],"derivedFrom":subQ14}),makeQuery(id+"F28.boolean.opBoolean","SPLIT",EDGE,{"disambiguationData":[TD([subQ5,subQ6,subQ8,subQ1,subQ10,subQ11,subQ12,subQ13])],"derivedFrom":subQ14})]});}
            var Q12;
            Q12=makeQuery(id+"F32.opExtrude","SWEPT_EDGE",EDGE,{"disambiguationData":[OSD([sQuery(id+"F31.wireOp",EDGE,"E140"),sQuery(id+"F31.wireOp",EDGE,"E142")])]});
            var Q13;
            Q13=makeQuery(id+"F32.opExtrude","SWEPT_EDGE",EDGE,{"disambiguationData":[OSD([sQuery(id+"F31.wireOp",EDGE,"E140"),sQuery(id+"F31.wireOp",EDGE,"E143")])]});
            fillet(context, id + "F33", {"entities" : qUnion([Q0, Q1, Q2, Q3, Q4, Q5, Q6, Q7, Q8, Q9, Q10, Q11, Q12, Q13]), "radius" : 5 * mm, "tangentPropagation" : true, "allowEdgeOverflow" : false});
        }
        {
            var Q0;
            Q0=makeQuery(id+"F32.opExtrude","SWEPT_EDGE",EDGE,{"disambiguationData":[OSD([sQuery(id+"F31.wireOp",EDGE,"E164"),sQuery(id+"F31.wireOp",EDGE,"E165")])]});
            var Q1;
            Q1=makeQuery(id+"F32.opExtrude","SWEPT_EDGE",EDGE,{"disambiguationData":[OSD([sQuery(id+"F31.wireOp",EDGE,"E162"),sQuery(id+"F31.wireOp",EDGE,"E165")])]});
            var Q2;
            Q2=makeQuery(id+"F32.opExtrude","SWEPT_EDGE",EDGE,{"disambiguationData":[OSD([sQuery(id+"F31.wireOp",EDGE,"E159"),sQuery(id+"F31.wireOp",EDGE,"E161")])]});
            var Q3;
            Q3=makeQuery(id+"F32.opExtrude","SWEPT_EDGE",EDGE,{"disambiguationData":[OSD([sQuery(id+"F31.wireOp",EDGE,"E160"),sQuery(id+"F31.wireOp",EDGE,"E161")])]});
            var Q4;
            Q4=makeQuery(id+"F32.opExtrude","SWEPT_EDGE",EDGE,{"disambiguationData":[OSD([sQuery(id+"F31.wireOp",EDGE,"E155"),sQuery(id+"F31.wireOp",EDGE,"E156")])]});
            var Q5;
            Q5=makeQuery(id+"F32.opExtrude","SWEPT_EDGE",EDGE,{"disambiguationData":[OSD([sQuery(id+"F31.wireOp",EDGE,"E153"),sQuery(id+"F31.wireOp",EDGE,"E156")])]});
            var Q6;
            Q6=makeQuery(id+"F32.opExtrude","SWEPT_EDGE",EDGE,{"disambiguationData":[OSD([sQuery(id+"F31.wireOp",EDGE,"E149"),sQuery(id+"F31.wireOp",EDGE,"E150")])]});
            var Q7;
            Q7=makeQuery(id+"F32.opExtrude","SWEPT_EDGE",EDGE,{"disambiguationData":[OSD([sQuery(id+"F31.wireOp",EDGE,"E149"),sQuery(id+"F31.wireOp",EDGE,"E152")])]});
            var Q8;
            Q8=makeQuery(id+"F32.opExtrude","SWEPT_EDGE",EDGE,{"disambiguationData":[OSD([sQuery(id+"F31.wireOp",EDGE,"E148.top"),sQuery(id+"F31.wireOp",EDGE,"E148.right")])]});
            var Q9;
            Q9=makeQuery(id+"F32.opExtrude","SWEPT_EDGE",EDGE,{"disambiguationData":[OSD([sQuery(id+"F31.wireOp",EDGE,"E148.top"),sQuery(id+"F31.wireOp",EDGE,"E148.left")])]});
            var Q10;
            Q10=makeQuery(id+"F32.opExtrude","SWEPT_EDGE",EDGE,{"disambiguationData":[OSD([sQuery(id+"F31.wireOp",EDGE,"E144"),sQuery(id+"F31.wireOp",EDGE,"E147")])]});
            var Q11;
            Q11=makeQuery(id+"F32.opExtrude","SWEPT_EDGE",EDGE,{"disambiguationData":[OSD([sQuery(id+"F31.wireOp",EDGE,"E141"),sQuery(id+"F31.wireOp",EDGE,"E142")])]});
            var Q12;
            Q12=makeQuery(id+"F32.opExtrude","SWEPT_EDGE",EDGE,{"disambiguationData":[OSD([sQuery(id+"F31.wireOp",EDGE,"E141"),sQuery(id+"F31.wireOp",EDGE,"E143")])]});
            var Q13;
            Q13=makeQuery(id+"F32.opExtrude","SWEPT_EDGE",EDGE,{"disambiguationData":[OSD([sQuery(id+"F31.wireOp",EDGE,"E146"),sQuery(id+"F31.wireOp",EDGE,"E147")])]});
            fillet(context, id + "F34", {"entities" : qUnion([Q0, Q1, Q2, Q3, Q4, Q5, Q6, Q7, Q8, Q9, Q10, Q11, Q12, Q13]), "radius" : 5 * mm, "tangentPropagation" : true, "allowEdgeOverflow" : false});
        }
    });
